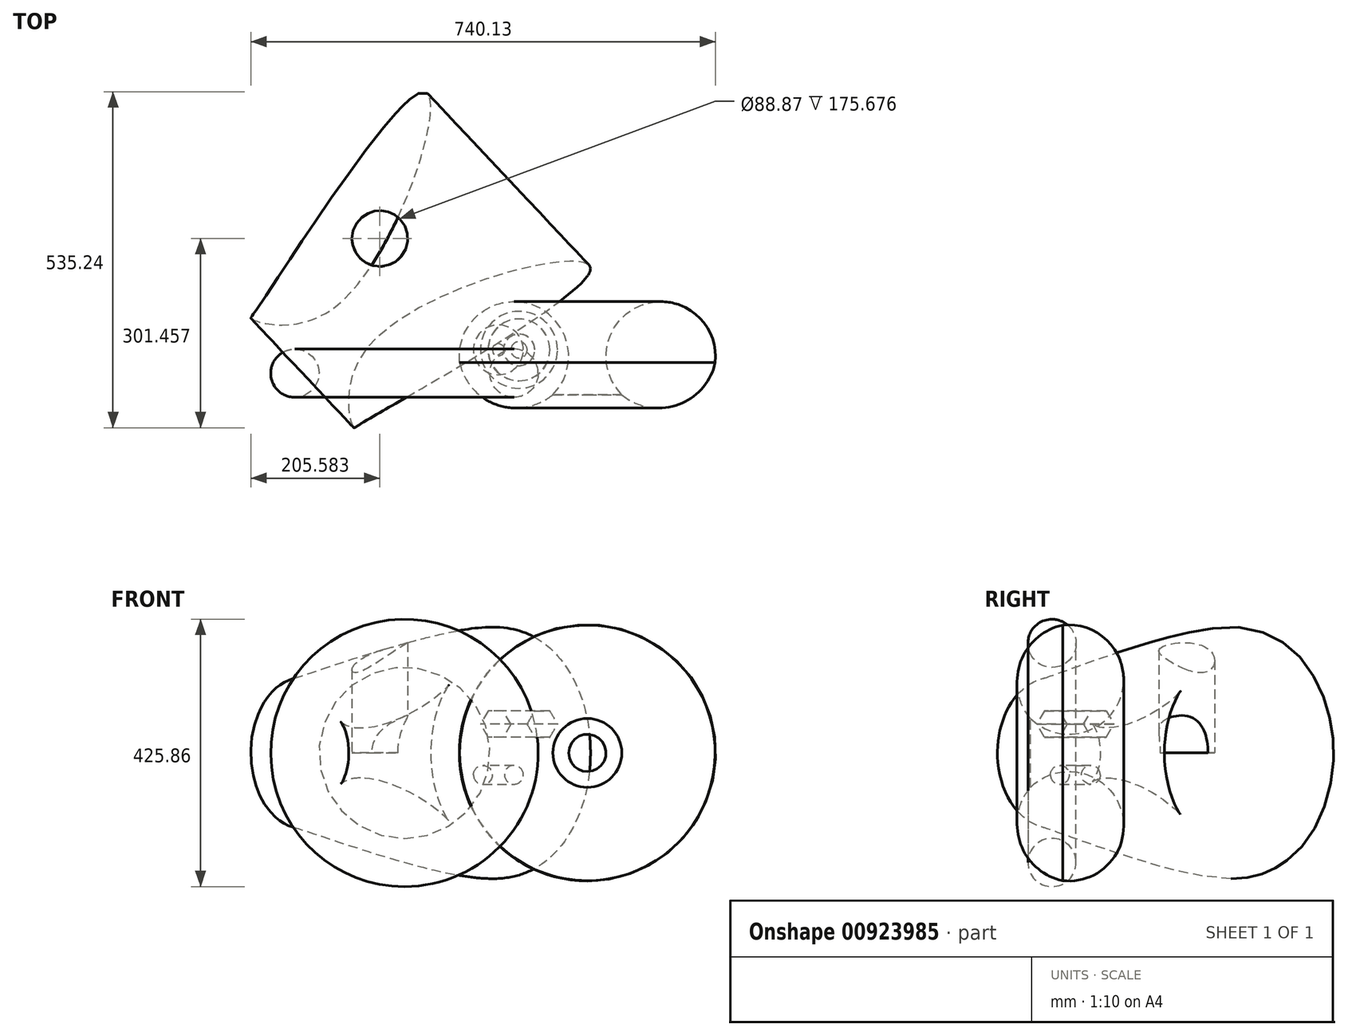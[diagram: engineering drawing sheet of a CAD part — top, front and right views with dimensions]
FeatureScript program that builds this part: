
annotation { "Feature Type Name" : "Feature", "Feature Type Description" : "" }
export const myFeature = defineFeature(function(context is Context, id is Id, definition is map)
    precondition{}
    {
        {
            var Q0;
            Q0=qCreatedBy(makeId("Front.planeOp"),FACE);
            var sketch = newSketch(context, id + "F0", { "sketchPlane" : qUnion([Q0])});
            skCircle(sketch, "E0", {"center": v(-49.63, -34.91) * mm, "radius": 15 * mm});
            skCircle(sketch, "E1", {"center": v(35.97, -33.9) * mm, "radius": 15 * mm});
            skLineSegment(sketch, "E2", {"start": v(-24.94, -32.06) * mm, "end": v(-24.94, -45.34) * mm});
            skLineSegment(sketch, "E3", {"start": v(62.97, -30.02) * mm, "end": v(62.97, -41) * mm});
            skSolve(sketch);
        }
        {
            var Q0;
            Q0=makeQuery(id+"F0.imprint","IMPRINT",FACE,{"disambiguationData":[TD([[makeQuery(id+"F0.imprint","IMPRINT",EDGE,{"derivedFrom":sQuery(id+"F0.wireOp",EDGE,"E0")}),1.0]])]});
            var Q1;
            Q1=sQuery(id+"F0.wireOp",EDGE,"E2");
            revolve(context, id + "F1", {"surfaceOperationType" : NewSurfaceOperationType.NEW, "entities" : qUnion([Q0]), "axis" : qUnion([Q1]), "revolveType" : RevolveType.FULL});
        }
        {
            var Q0;
            Q0=qCreatedBy(makeId("Front.planeOp"),FACE);
            var sketch = newSketch(context, id + "F2", { "sketchPlane" : qUnion([Q0])});
            skCircle(sketch, "E4.cCircle", {"center": v(44.98, 45.9) * mm, "radius": 20.93 * mm, "construction": true});
            skLineSegment(sketch, "E4.0", {"start": v(32.98, 24.93) * mm, "end": v(20.82, 45.81) * mm});
            skLineSegment(sketch, "E4.1", {"start": v(20.82, 45.81) * mm, "end": v(32.82, 66.78) * mm});
            skLineSegment(sketch, "E4.2", {"start": v(32.82, 66.78) * mm, "end": v(56.99, 66.87) * mm});
            skLineSegment(sketch, "E4.3", {"start": v(56.99, 66.87) * mm, "end": v(69.15, 45.99) * mm});
            skLineSegment(sketch, "E4.4", {"start": v(69.15, 45.99) * mm, "end": v(57.14, 25.02) * mm});
            skLineSegment(sketch, "E4.5", {"start": v(57.14, 25.02) * mm, "end": v(32.98, 24.93) * mm});
            skPoint(sketch, "E4.0.midPoint", {"position": v(26.9, 35.37) * mm});
            skLineSegment(sketch, "E5", {"start": v(7.9, 40.4) * mm, "end": v(7.9, 20.95) * mm});
            skSolve(sketch);
        }
        {
            var Q0;
            Q0=makeQuery(id+"F2.imprint","IMPRINT",FACE,{"disambiguationData":[TD([[makeQuery(id+"F2.imprint","IMPRINT",EDGE,{"derivedFrom":sQuery(id+"F2.wireOp",EDGE,"E4.0")}),-1.0]])]});
            var Q1;
            Q1=sQuery(id+"F2.wireOp",EDGE,"E5");
            revolve(context, id + "F3", {"surfaceOperationType" : NewSurfaceOperationType.NEW, "entities" : qUnion([Q0]), "axis" : qUnion([Q1]), "revolveType" : RevolveType.FULL});
        }
        {
            var Q0;
            Q0=qCreatedBy(makeId("Top.planeOp"),FACE);
            var sketch = newSketch(context, id + "F4", { "sketchPlane" : qUnion([Q0])});
            skArc(sketch, "E6", {"start": v(-86.65, -20.26) * mm, "mid": v(-26.8, -87.73) * mm, "end": v(61.92, -71.54) * mm});
            skArc(sketch, "E7", {"start": v(61.92, -71.54) * mm, "mid": v(28.37, 72.1) * mm, "end": v(-86.65, -20.26) * mm});
            skArc(sketch, "E8", {"start": v(-27.26, -71.54) * mm, "mid": v(-4.28, -85.32) * mm, "end": v(18.7, -71.54) * mm});
            skLineSegment(sketch, "E9", {"start": v(116.8, -46.98) * mm, "end": v(116.8, -14.93) * mm});
            skSolve(sketch);
        }
        {
            var Q0;
            Q0=makeQuery(id+"F4.imprint","IMPRINT",FACE,{"disambiguationData":[TD([[makeQuery(id+"F4.imprint","IMPRINT",EDGE,{"derivedFrom":sQuery(id+"F4.wireOp",EDGE,"E6")}),1.0]])]});
            var sketch = newSketch(context, id + "F5", { "sketchPlane" : qUnion([Q0])});
            skSolve(sketch);
        }
        {
            var Q0;
            Q0=makeQuery(id+"F5.imprint","IMPRINT",FACE,{"disambiguationData":[TD([[makeQuery(id+"F5.imprint","IMPRINT",EDGE,{"derivedFrom":makeQuery(id+"F4.imprint","IMPRINT",EDGE,{"derivedFrom":sQuery(id+"F4.wireOp",EDGE,"E6")})}),1.0]])]});
            var Q1;
            Q1=sQuery(id+"F4.wireOp",EDGE,"E9");
            revolve(context, id + "F6", {"surfaceOperationType" : NewSurfaceOperationType.NEW, "entities" : qUnion([Q0]), "axis" : qUnion([Q1]), "revolveType" : RevolveType.FULL});
        }
        {
            var Q0;
            Q0=qCreatedBy(makeId("Top.planeOp"),FACE);
            var sketch = newSketch(context, id + "F7", { "sketchPlane" : qUnion([Q0])});
            skCircle(sketch, "E10", {"center": v(0, -37.18) * mm, "radius": 38.37 * mm});
            skLineSegment(sketch, "E11", {"start": v(-174.55, -43.06) * mm, "end": v(-174.55, 0) * mm});
            skSolve(sketch);
        }
        {
            var Q0;
            Q0 = qSketchRegion(id + "F7", true);
            var Q1;
            Q1=sQuery(id+"F7.wireOp",EDGE,"E11");
            revolve(context, id + "F8", {"surfaceOperationType" : NewSurfaceOperationType.NEW, "entities" : qUnion([Q0]), "axis" : qUnion([Q1]), "revolveType" : RevolveType.FULL});
        }
        {
            var Q0;
            Q0=qCreatedBy(makeId("Top.planeOp"),FACE);
            var sketch = newSketch(context, id + "F9", { "sketchPlane" : qUnion([Q0])});
            skFitSpline(sketch, "E12", {"points": [v(-227.36, 10.95) * mm, v(121.72, 129.1) * mm, v(-248.35, -120.4) * mm, v(-256.15, -122.8) * mm, v(-227.36, 10.95) * mm]});
            skLineSegment(sketch, "E13", {"start": v(-217.38, 75.94) * mm, "end": v(-163.92, 126.23) * mm});
            skSolve(sketch);
        }
        {
            var Q0;
            Q0 = qSketchRegion(id + "F9", true);
            var Q1;
            Q1=sQuery(id+"F9.wireOp",EDGE,"E13");
            revolve(context, id + "F10", {"surfaceOperationType" : NewSurfaceOperationType.NEW, "entities" : qUnion([Q0]), "axis" : qUnion([Q1]), "revolveType" : RevolveType.FULL});
        }
        {
            var Q0;
            Q0=qCreatedBy(makeId("Top.planeOp"),FACE);
            var sketch = newSketch(context, id + "F11", { "sketchPlane" : qUnion([Q0])});
            skCircle(sketch, "E14", {"center": v(-213.72, 177.38) * mm, "radius": 44.44 * mm});
            skSolve(sketch);
        }
        {
            var Q0;
            Q0 = qSketchRegion(id + "F11", true);
            extrude(context, id + "F12", {"entities" : qUnion([Q0]), "operationType" : NewBodyOperationType.REMOVE, "depth" : 1785 * mm, "offsetDistance" : 25 * mm});
        }
    });
